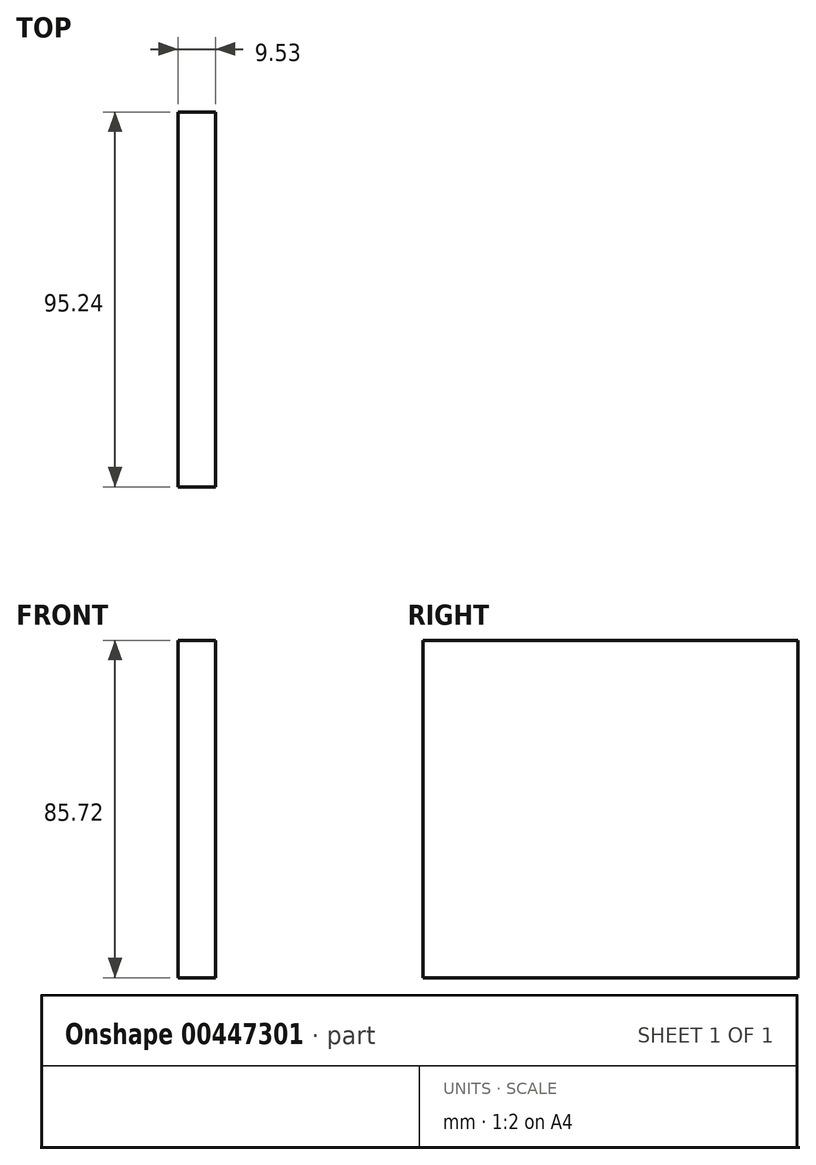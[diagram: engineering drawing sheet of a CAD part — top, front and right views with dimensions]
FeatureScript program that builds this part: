
annotation { "Feature Type Name" : "Feature", "Feature Type Description" : "" }
export const myFeature = defineFeature(function(context is Context, id is Id, definition is map)
    precondition{}
    {
        {
            var Q0;
            Q0=qCreatedBy(makeId("Right.planeOp"),FACE);
            var sketch = newSketch(context, id + "F0", { "sketchPlane" : qUnion([Q0])});
            skLineSegment(sketch, "E0.bottom", {"start": v(-47.63, -42.86) * mm, "end": v(47.63, -42.86) * mm});
            skLineSegment(sketch, "E0.top", {"start": v(-47.63, 42.86) * mm, "end": v(47.63, 42.86) * mm});
            skLineSegment(sketch, "E0.left", {"start": v(-47.63, -42.86) * mm, "end": v(-47.63, 42.86) * mm});
            skLineSegment(sketch, "E0.right", {"start": v(47.63, -42.86) * mm, "end": v(47.63, 42.86) * mm});
            skPoint(sketch, "E0.middle", {"position": v(0, 0) * mm});
            skSolve(sketch);
        }
        {
            var Q0;
            Q0=makeQuery(id+"F0.imprint","IMPRINT",FACE,{"disambiguationData":[TD([[makeQuery(id+"F0.imprint","IMPRINT",EDGE,{"derivedFrom":sQuery(id+"F0.wireOp",EDGE,"E0.bottom")}),1.0]])]});
            extrude(context, id + "F1", {"entities" : qUnion([Q0]), "depth" : 9.52 * mm});
        }
    });
